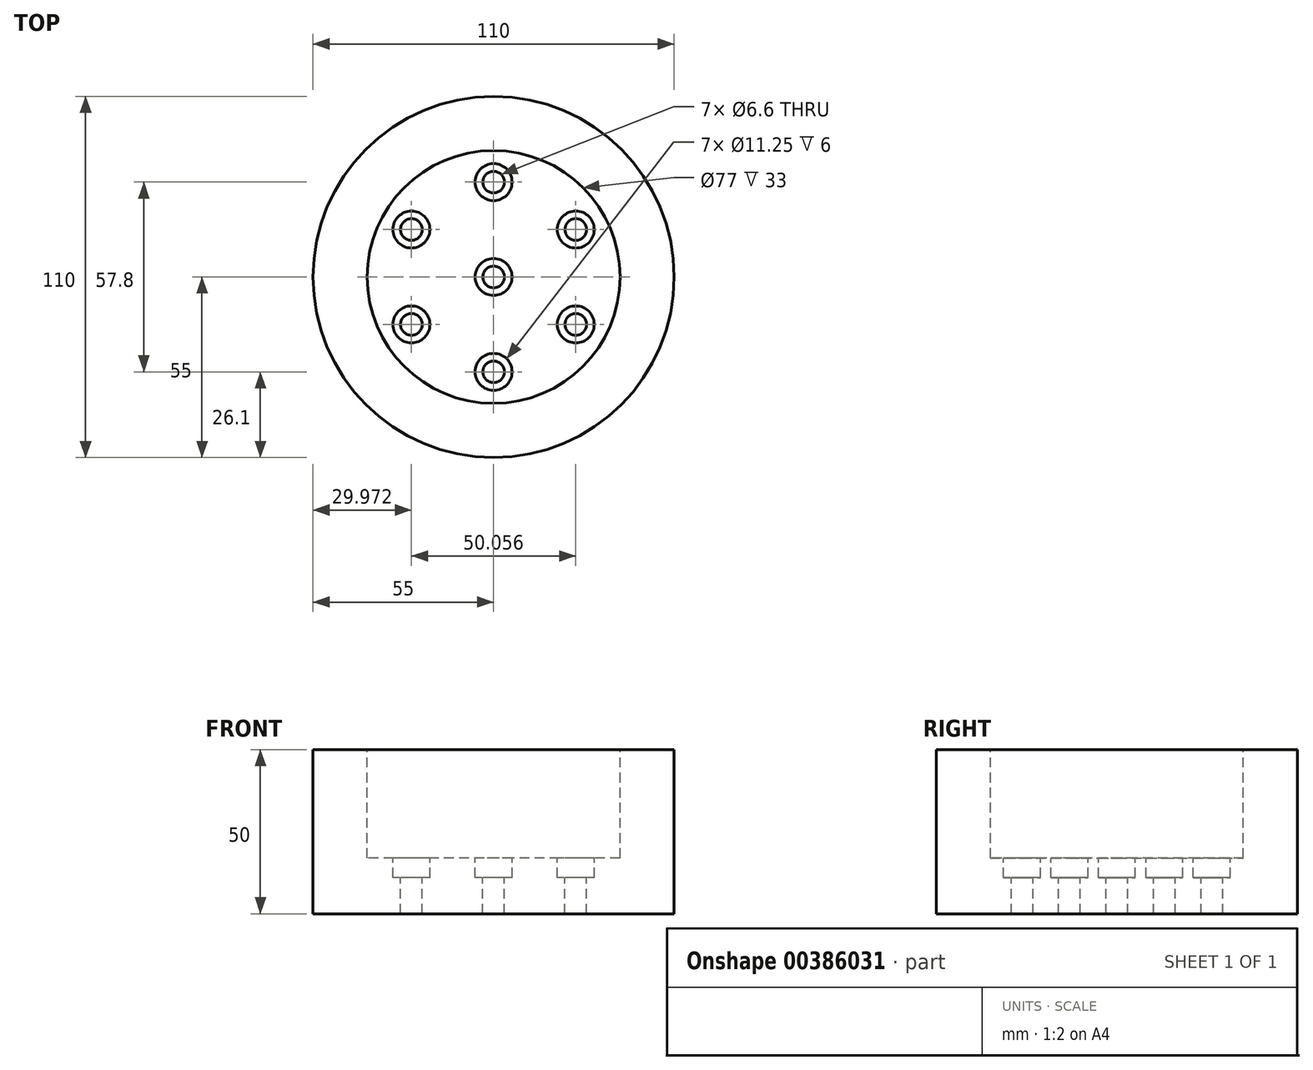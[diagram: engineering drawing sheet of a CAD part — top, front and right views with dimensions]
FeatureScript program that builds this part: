
annotation { "Feature Type Name" : "Feature", "Feature Type Description" : "" }
export const myFeature = defineFeature(function(context is Context, id is Id, definition is map)
    precondition{}
    {
        {
            var Q0;
            Q0=qCreatedBy(makeId("Top.planeOp"),FACE);
            var sketch = newSketch(context, id + "F0", { "sketchPlane" : qUnion([Q0])});
            skCircle(sketch, "E0", {"center": v(0, 0) * mm, "radius": 55 * mm});
            skCircle(sketch, "E1.cCircle", {"center": v(0, 0) * mm, "radius": 25.03 * mm, "construction": true});
            skLineSegment(sketch, "E1.0", {"start": v(25.03, -14.45) * mm, "end": v(0, -28.9) * mm});
            skLineSegment(sketch, "E1.1", {"start": v(0, -28.9) * mm, "end": v(-25.03, -14.45) * mm});
            skLineSegment(sketch, "E1.2", {"start": v(-25.03, -14.45) * mm, "end": v(-25.03, 14.45) * mm});
            skLineSegment(sketch, "E1.3", {"start": v(-25.03, 14.45) * mm, "end": v(0, 28.9) * mm});
            skLineSegment(sketch, "E1.4", {"start": v(0, 28.9) * mm, "end": v(25.03, 14.45) * mm});
            skLineSegment(sketch, "E1.5", {"start": v(25.03, 14.45) * mm, "end": v(25.03, -14.45) * mm});
            skPoint(sketch, "E1.0.midPoint", {"position": v(12.51, -21.67) * mm});
            skCircle(sketch, "E2", {"center": v(-25.03, 14.45) * mm, "radius": 3 * mm});
            skCircle(sketch, "E3", {"center": v(0, 28.9) * mm, "radius": 3 * mm});
            skCircle(sketch, "E4", {"center": v(25.03, 14.45) * mm, "radius": 3 * mm});
            skCircle(sketch, "E5", {"center": v(25.03, -14.45) * mm, "radius": 3 * mm});
            skCircle(sketch, "E6", {"center": v(0, -28.9) * mm, "radius": 3 * mm});
            skCircle(sketch, "E7", {"center": v(-25.03, -14.45) * mm, "radius": 3 * mm});
            skCircle(sketch, "E8", {"center": v(0, 0) * mm, "radius": 3 * mm});
            skSolve(sketch);
        }
        {
            var Q0;
            Q0=makeQuery(id+"F0.imprint","IMPRINT",FACE,{"disambiguationData":[TD([[makeQuery(id+"F0.imprint","IMPRINT",EDGE,{"derivedFrom":sQuery(id+"F0.wireOp",EDGE,"E0")}),1.0]])]});
            var Q1;
            Q1=makeQuery(id+"F0.imprint","IMPRINT",FACE,{"disambiguationData":[TD([[makeQuery(id+"F0.imprint","IMPRINT",EDGE,{"derivedFrom":sQuery(id+"F0.wireOp",EDGE,"E8")}),-1.0]])]});
            extrude(context, id + "F1", {"entities" : qUnion([Q0, Q1]), "depth" : 50 * mm, "offsetDistance" : 25 * mm});
        }
        {
            var Q0;
            Q0=makeQuery(id+"F1.opExtrude","CAP_FACE",FACE,{"disambiguationData":[OSD([sQuery(id+"F0.wireOp",EDGE,"E0")])],"isStart":false});
            var sketch = newSketch(context, id + "F2", { "sketchPlane" : qUnion([Q0])});
            skCircle(sketch, "E9", {"center": v(0, 0) * mm, "radius": 38.5 * mm});
            skSolve(sketch);
        }
        {
            var Q0;
            Q0=makeQuery(id+"F2.imprint","IMPRINT",FACE,{"disambiguationData":[TD([[makeQuery(id+"F2.imprint","IMPRINT",EDGE,{"derivedFrom":sQuery(id+"F2.wireOp",EDGE,"E9")}),1.0]])]});
            extrude(context, id + "F3", {"entities" : qUnion([Q0]), "operationType" : NewBodyOperationType.REMOVE, "oppositeDirection" : true, "depth" : 33 * mm, "offsetDistance" : 25 * mm});
        }
        {
            var Q0;
            Q0=makeQuery(id+"F3.boolean.opBoolean","COPY",FACE,{"derivedFrom":makeQuery(id+"F3.opExtrude","CAP_FACE",FACE,{"disambiguationData":[OSD([sQuery(id+"F0.wireOp",EDGE,"E2"),sQuery(id+"F0.wireOp",EDGE,"E3"),sQuery(id+"F0.wireOp",EDGE,"E4"),sQuery(id+"F0.wireOp",EDGE,"E5"),sQuery(id+"F0.wireOp",EDGE,"E6"),sQuery(id+"F0.wireOp",EDGE,"E7"),sQuery(id+"F0.wireOp",EDGE,"E8"),sQuery(id+"F2.wireOp",EDGE,"E9")])],"isStart":false})});
            var sketch = newSketch(context, id + "F4", { "sketchPlane" : qUnion([Q0])});
            skCircle(sketch, "E10.cCircle", {"center": v(0, 0) * mm, "radius": 25.03 * mm, "construction": true});
            skLineSegment(sketch, "E10.0", {"start": v(25.03, 14.45) * mm, "end": v(25.03, -14.45) * mm});
            skLineSegment(sketch, "E10.1", {"start": v(25.03, -14.45) * mm, "end": v(0, -28.9) * mm});
            skLineSegment(sketch, "E10.2", {"start": v(0, -28.9) * mm, "end": v(-25.03, -14.45) * mm});
            skLineSegment(sketch, "E10.3", {"start": v(-25.03, -14.45) * mm, "end": v(-25.03, 14.45) * mm});
            skLineSegment(sketch, "E10.4", {"start": v(-25.03, 14.45) * mm, "end": v(0, 28.9) * mm});
            skLineSegment(sketch, "E10.5", {"start": v(0, 28.9) * mm, "end": v(25.03, 14.45) * mm});
            skPoint(sketch, "E10.0.midPoint", {"position": v(25.03, 0) * mm});
            skSolve(sketch);
        }
        {
            var Q0;
            Q0=sQuery(id+"F4.wireOp",VERTEX,"E10.4.start");
            var Q1;
            Q1=sQuery(id+"F4.wireOp",VERTEX,"E10.3.start");
            var Q2;
            Q2=sQuery(id+"F4.wireOp",VERTEX,"E10.2.start");
            var Q3;
            Q3=sQuery(id+"F4.wireOp",VERTEX,"E10.1.start");
            var Q4;
            Q4=sQuery(id+"F4.wireOp",VERTEX,"E10.0.start");
            var Q5;
            Q5=sQuery(id+"F4.wireOp",VERTEX,"E10.5.start");
            var Q6;
            Q6=sQuery(id+"F4.wireOp",VERTEX,"E10.cCircle.center");
            var Q7;
            Q7=makeQuery(id+"F1.opExtrude","SWEPT_BODY",BODY,{"disambiguationData":[OSD([sQuery(id+"F0.wireOp",EDGE,"E0"),sQuery(id+"F0.wireOp",EDGE,"E2"),sQuery(id+"F0.wireOp",EDGE,"E3"),sQuery(id+"F0.wireOp",EDGE,"E4"),sQuery(id+"F0.wireOp",EDGE,"E5"),sQuery(id+"F0.wireOp",EDGE,"E6"),sQuery(id+"F0.wireOp",EDGE,"E7"),sQuery(id+"F0.wireOp",EDGE,"E8")])]});
            hole(context, id + "F5", {"style" : HoleStyle.C_BORE, "endStyle" : HoleEndStyle.THROUGH, "standardTappedOrClearance" : lookupTablePath({ "standard" : "ISO", "fit" : "Normal", "size" : "M6", "type" : "Clearance" }), "standardBlindInLast" : lookupTablePath({ "fit" : "Standard", "standard" : "ISO", "size" : "M6", "type" : "Clearance" }), "holeDiameter" : 6.6 * mm, "cBoreDiameter" : 11.25 * mm, "cBoreDepth" : 6 * mm, "isTappedThrough" : true, "tappedDepth" : 12 * mm, "tapClearance" : 3, "locations" : qUnion([Q0, Q1, Q2, Q3, Q4, Q5, Q6]), "scope" : qUnion([Q7])});
        }
    });
